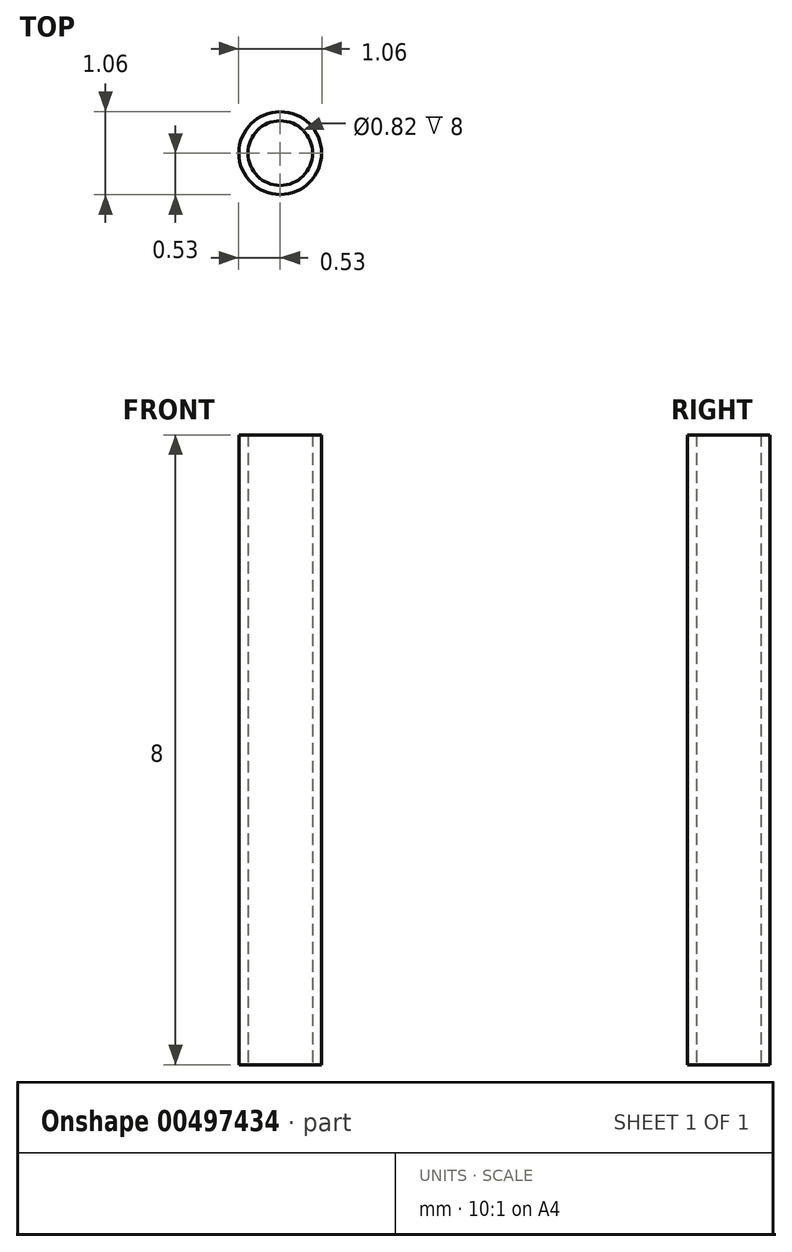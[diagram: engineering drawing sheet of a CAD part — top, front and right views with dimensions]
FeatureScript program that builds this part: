
annotation { "Feature Type Name" : "Feature", "Feature Type Description" : "" }
export const myFeature = defineFeature(function(context is Context, id is Id, definition is map)
    precondition{}
    {
        {
            var Q0;
            Q0=qCreatedBy(makeId("Top.planeOp"),FACE);
            var sketch = newSketch(context, id + "F0", { "sketchPlane" : qUnion([Q0])});
            skCircle(sketch, "E0", {"center": v(0, 0) * mm, "radius": 0.41 * mm});
            skCircle(sketch, "E1", {"center": v(0, 0) * mm, "radius": 0.53 * mm});
            skSolve(sketch);
        }
        {
            var Q0;
            Q0=makeQuery(id+"F0.imprint","IMPRINT",FACE,{"disambiguationData":[TD([[makeQuery(id+"F0.imprint","IMPRINT",EDGE,{"derivedFrom":sQuery(id+"F0.wireOp",EDGE,"E0")}),-1.0]])]});
            extrude(context, id + "F1", {"entities" : qUnion([Q0]), "depth" : 8 * mm});
        }
    });
